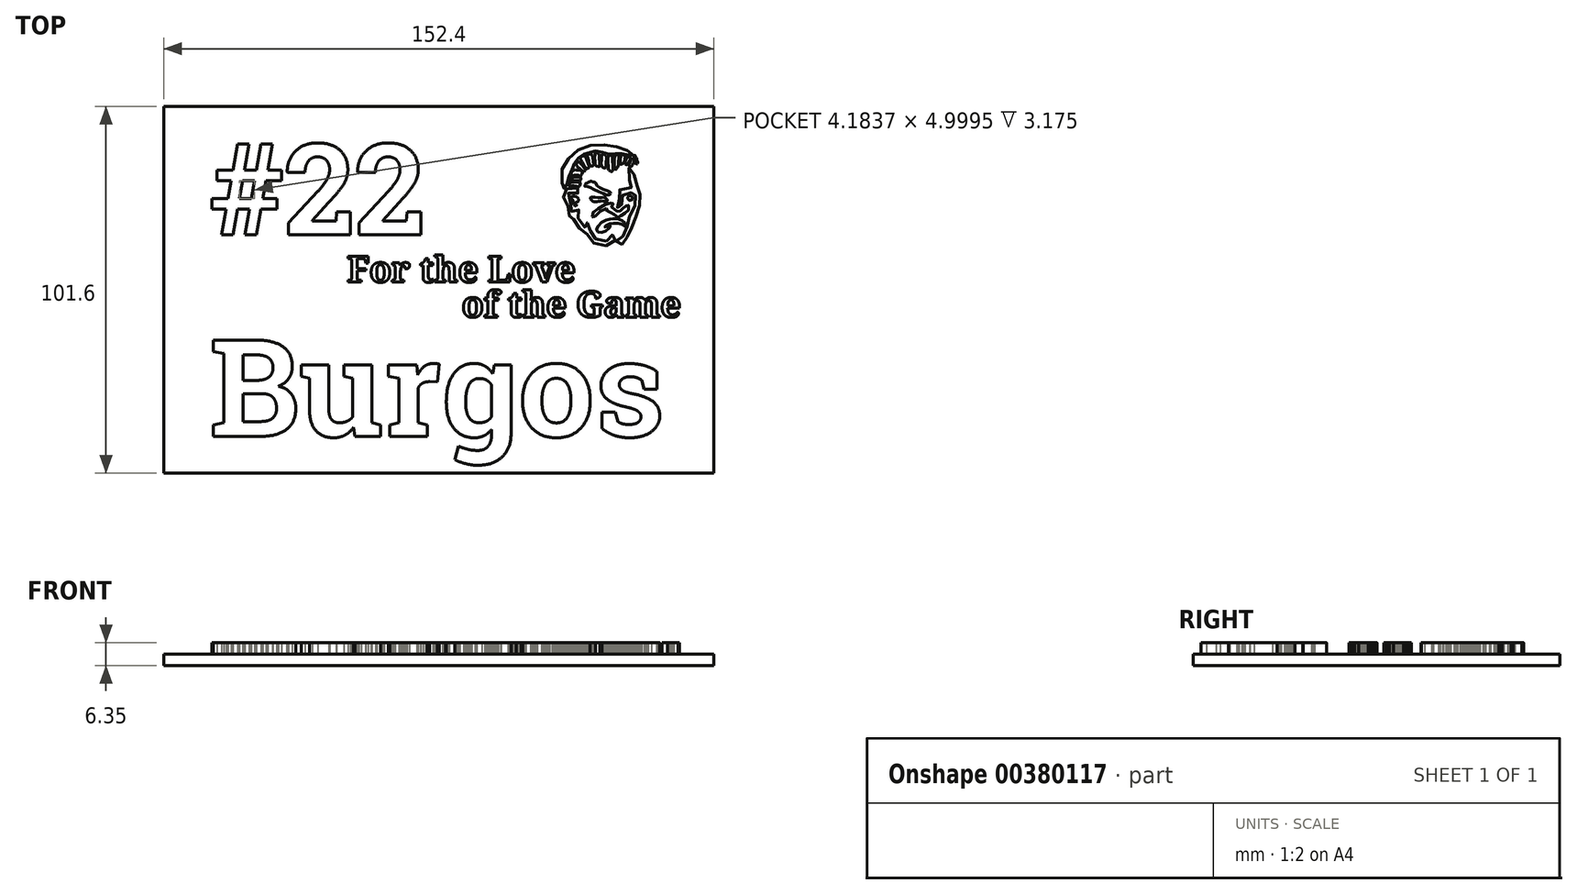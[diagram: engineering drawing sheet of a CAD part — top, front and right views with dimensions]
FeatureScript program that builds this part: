
annotation { "Feature Type Name" : "Feature", "Feature Type Description" : "" }
export const myFeature = defineFeature(function(context is Context, id is Id, definition is map)
    precondition{}
    {
        {
            var Q0;
            Q0=qCreatedBy(makeId("Top.planeOp"),FACE);
            var sketch = newSketch(context, id + "F0", { "sketchPlane" : qUnion([Q0])});
            skLineSegment(sketch, "E0.bottom", {"start": v(-75.13, 26) * mm, "end": v(77.27, 26) * mm});
            skLineSegment(sketch, "E0.top", {"start": v(-75.13, -75.6) * mm, "end": v(77.27, -75.6) * mm});
            skLineSegment(sketch, "E0.left", {"start": v(-75.13, 26) * mm, "end": v(-75.13, -75.6) * mm});
            skLineSegment(sketch, "E0.right", {"start": v(77.27, 26) * mm, "end": v(77.27, -75.6) * mm});
            skSolve(sketch);
        }
        {
            var Q0;
            Q0=makeQuery(id+"F0.imprint","IMPRINT",FACE,{"disambiguationData":[TD([[makeQuery(id+"F0.imprint","IMPRINT",EDGE,{"derivedFrom":sQuery(id+"F0.wireOp",EDGE,"E0.bottom")}),-1.0]])]});
            var sketch = newSketch(context, id + "F1", { "sketchPlane" : qUnion([Q0])});
            skText(sketch, "E1", { "text": "Burgos", "fontName": "RobotoSlab-Bold.ttf"});
            skText(sketch, "E2", { "text": "#22", "fontName": "RobotoSlab-Bold.ttf"});
            skFitSpline(sketch, "E3", {"points": [v(47.57, -11.3) * mm, v(48.35, -11.04) * mm, v(48.7, -10.35) * mm, v(49.04, -9.7) * mm, v(49.57, -9.46) * mm, v(50.02, -9.78) * mm, v(50.06, -10.58) * mm, v(49.74, -11.5) * mm, v(49.1, -12.15) * mm, v(47.63, -12.55) * mm, v(46.12, -12.5) * mm, v(44.61, -12.12) * mm, v(43.38, -11.34) * mm, v(42.6, -10.32) * mm, v(42.24, -9.52) * mm, v(42.15, -9.31) * mm, v(41.34, -8.82) * mm, v(40.33, -8.02) * mm, v(39.44, -7.2) * mm, v(38.67, -6.1) * mm, v(38.42, -5) * mm, v(38.42, -4.22) * mm, v(38.35, -4.2) * mm, v(37.68, -4.39) * mm, v(37.16, -4.27) * mm, v(36.95, -3.72) * mm, v(36.86, -2.5) * mm, v(36.8, -1.48) * mm, v(36.67, -1.07) * mm, v(35.77, 0.2) * mm, v(35.58, 1.07) * mm, v(35.86, 2.13) * mm, v(36.18, 2.7) * mm, v(36.53, 3.12) * mm, v(37.23, 3.22) * mm, v(39.03, 3.4) * mm, v(39.82, 3.34) * mm, v(40.19, 3.09) * mm, v(40.23, 2.45) * mm, v(39.66, 1.98) * mm, v(38.93, 1.9) * mm, v(38.59, 2.03) * mm, v(37.24, 2.03) * mm, v(36.72, 1.65) * mm, v(36.72, 0.85) * mm, v(37.32, -0.2) * mm, v(37.77, -1.18) * mm, v(37.85, -2.09) * mm, v(37.9, -3.1) * mm, v(37.99, -3.1) * mm, v(38.63, -3.1) * mm, v(39.4, -2.76) * mm, v(39.72, -2.59) * mm, v(39.8, -2.7) * mm, v(39.73, -3.22) * mm, v(39.6, -4) * mm, v(39.6, -4.77) * mm, v(40.1, -5.82) * mm, v(41.16, -7.15) * mm, v(41.6, -7.53) * mm, v(41.9, -7.56) * mm, v(41.89, -7.44) * mm, v(41.82, -6.61) * mm, v(42, -6.23) * mm, v(42.5, -6.3) * mm, v(42.8, -6.61) * mm, v(43.05, -7.98) * mm, v(43.22, -8.82) * mm, v(43.51, -9.54) * mm, v(44.12, -10.4) * mm, v(45.11, -11.01) * mm, v(46.32, -11.33) * mm, v(47.57, -11.3) * mm]});
            skFitSpline(sketch, "E4", {"points": [v(47.8, -7.3) * mm, v(47.13, -7.42) * mm, v(47.01, -7.42) * mm, v(47.13, -7.18) * mm, v(48.11, -6.65) * mm, v(49.11, -6.46) * mm, v(50.54, -6.45) * mm, v(51.76, -6.67) * mm, v(52.61, -7.21) * mm, v(52.82, -7.33) * mm, v(52.97, -7.12) * mm, v(52.7, -6.5) * mm, v(52.11, -5.74) * mm, v(50.6, -5.18) * mm, v(49.08, -5.16) * mm, v(48.46, -5.24) * mm, v(47.16, -5.6) * mm, v(45.65, -6.61) * mm, v(44.86, -7.78) * mm, v(44.9, -8.5) * mm, v(45.47, -8.94) * mm, v(46.7, -8.8) * mm, v(47.75, -8.16) * mm, v(48.56, -7.4) * mm, v(48.6, -7.12) * mm, v(47.8, -7.3) * mm]});
            skFitSpline(sketch, "E5", {"points": [v(51.85, -12.22) * mm, v(51.05, -12.44) * mm, v(50.33, -12.28) * mm, v(50.13, -11.73) * mm, v(50.52, -11.04) * mm, v(51.15, -10.86) * mm, v(51.76, -10.57) * mm, v(52.13, -10) * mm, v(52.3, -9.2) * mm, v(52.67, -8.25) * mm, v(53.2, -7.5) * mm, v(53.55, -6.76) * mm, v(53.63, -5.82) * mm, v(53.78, -4.85) * mm, v(54.49, -3.73) * mm, v(55.3, -2.73) * mm, v(55.42, -1.6) * mm, v(55.17, -0.4) * mm, v(55.2, 0.11) * mm, v(55.52, 1.32) * mm, v(55.57, 2.16) * mm, v(55.47, 2.42) * mm, v(54.99, 2.38) * mm, v(54.56, 2.14) * mm, v(53.7, 2.1) * mm, v(52.55, 2.06) * mm, v(52.07, 1.77) * mm, v(51.98, 1.02) * mm, v(52.2, 0.28) * mm, v(52.08, -0.6) * mm, v(51.72, -1.24) * mm, v(51.47, -1.75) * mm, v(51.5, -2.22) * mm, v(51.32, -2.4) * mm, v(50.6, -2.13) * mm, v(50.38, -1.6) * mm, v(50.64, -0.97) * mm, v(51, -0.17) * mm, v(51.06, 0.44) * mm, v(50.78, 1.07) * mm, v(50.66, 1.97) * mm, v(51.18, 2.9) * mm, v(52.12, 3.24) * mm, v(53.3, 3.36) * mm, v(54.52, 3.48) * mm, v(54.66, 3.6) * mm, v(54.38, 3.97) * mm, v(54, 4.8) * mm, v(53.79, 6.28) * mm, v(53.9, 7.94) * mm, v(53.79, 8.9) * mm, v(53.79, 9.1) * mm, v(54.03, 9.04) * mm, v(54.76, 8.52) * mm, v(55.13, 7.38) * mm, v(55.34, 5.97) * mm, v(55.56, 4.72) * mm, v(56.14, 3.87) * mm, v(56.71, 3.56) * mm, v(57.08, 2.91) * mm, v(56.95, 1.93) * mm, v(56.51, 0.55) * mm, v(56.4, -0.31) * mm, v(56.62, -1.36) * mm, v(56.69, -2.19) * mm, v(56.32, -3.56) * mm, v(55.4, -4.86) * mm, v(54.62, -5.8) * mm, v(54.5, -7.08) * mm, v(54.37, -8.24) * mm, v(53.76, -9.26) * mm, v(53.43, -9.82) * mm, v(53.28, -10.59) * mm, v(53.14, -11.27) * mm, v(52.34, -11.95) * mm, v(51.85, -12.22) * mm]});
            skFitSpline(sketch, "E6", {"points": [v(51.65, -4.28) * mm, v(52.13, -3.81) * mm, v(53.02, -3.37) * mm, v(53.66, -2.72) * mm, v(53.77, -1.9) * mm, v(53.38, -1.13) * mm, v(53.21, -1.15) * mm, v(53, -1.68) * mm, v(52.43, -2.14) * mm, v(51.8, -2.46) * mm, v(51.42, -2.92) * mm, v(50.93, -3.27) * mm, v(50.6, -3.17) * mm, v(50.13, -2.68) * mm, v(49.7, -2.46) * mm, v(49.28, -2.45) * mm, v(49, -1.98) * mm, v(49.06, -1.41) * mm, v(49.39, -0.94) * mm, v(49.4, -0.71) * mm, v(48.82, -0.74) * mm, v(47.56, -0.99) * mm, v(45.6, -2.02) * mm, v(44.06, -3.24) * mm, v(43.57, -3.77) * mm, v(43.7, -4.86) * mm, v(43.9, -4.88) * mm, v(44.45, -4.27) * mm, v(46.1, -2.93) * mm, v(47.41, -2.3) * mm, v(47.63, -2.3) * mm, v(47.73, -2.85) * mm, v(48.15, -3.33) * mm, v(48.9, -3.44) * mm, v(49.24, -3.55) * mm, v(49.84, -4.18) * mm, v(50.54, -4.68) * mm, v(51.18, -4.66) * mm, v(51.65, -4.28) * mm]});
            skFitSpline(sketch, "E7", {"points": [v(54.73, 0.39) * mm, v(54.77, 0.82) * mm, v(54.18, 1.2) * mm, v(53.55, 1.02) * mm, v(53.47, 0.3) * mm, v(54.02, 0) * mm, v(54.73, 0.39) * mm]});
            skFitSpline(sketch, "E8", {"points": [v(44.44, -0.47) * mm, v(43.66, -0.25) * mm, v(43.08, 0.44) * mm, v(43.14, 0.75) * mm, v(43.78, 0.8) * mm, v(46.74, 0.78) * mm, v(47.17, 0.7) * mm, v(47.78, -0.13) * mm, v(47.64, -0.32) * mm, v(46.64, -0.26) * mm, v(45.29, -0.32) * mm, v(44.44, -0.47) * mm]});
            skFitSpline(sketch, "E9", {"points": [v(46.65, 1.86) * mm, v(47.46, 1.48) * mm, v(48.33, 1.53) * mm, v(48.69, 2.02) * mm, v(48.54, 2.32) * mm, v(47.26, 2.83) * mm, v(45.32, 3.72) * mm, v(44.79, 4.23) * mm, v(44.53, 4.83) * mm, v(44.13, 5) * mm, v(43.88, 5) * mm, v(43.34, 5.26) * mm, v(43.09, 5.3) * mm, v(42.9, 5.05) * mm, v(42.6, 5.07) * mm, v(42.3, 4.85) * mm, v(42.2, 4.73) * mm, v(41.9, 4.72) * mm, v(41.8, 4.5) * mm, v(41.38, 4.05) * mm, v(41.56, 3.84) * mm, v(42.59, 3.74) * mm, v(43.78, 3.19) * mm, v(46.65, 1.86) * mm]});
            skFitSpline(sketch, "E10", {"points": [v(39.09, -1.2) * mm, v(38.85, -1.02) * mm, v(39.04, -0.63) * mm, v(39.6, -0.4) * mm, v(39.72, 0.33) * mm, v(39.01, 1.06) * mm, v(38.23, 1.1) * mm, v(37.7, 0.65) * mm, v(37.83, 0.29) * mm, v(38.12, 0.15) * mm, v(38.31, -0.34) * mm, v(38.52, -1.23) * mm, v(38.92, -1.63) * mm, v(39.18, -1.51) * mm, v(39.26, -1.2) * mm, v(39.09, -1.2) * mm]});
            skFitSpline(sketch, "E11", {"points": [v(35.18, 4.73) * mm, v(35.4, 3.4) * mm, v(35.76, 3.05) * mm, v(35.87, 3.13) * mm, v(36.08, 3.42) * mm, v(36.43, 3.67) * mm, v(36.66, 4.42) * mm, v(36.6, 5.36) * mm, v(37.02, 6.1) * mm, v(37.15, 6.7) * mm, v(37.23, 7.46) * mm, v(37.88, 8.4) * mm, v(38.45, 9.02) * mm, v(38.56, 9.75) * mm, v(38.74, 10.4) * mm, v(39.17, 10.98) * mm, v(39.64, 11.29) * mm, v(39.78, 11.9) * mm, v(40.12, 12.28) * mm, v(40.85, 12.68) * mm, v(41.65, 12.77) * mm, v(42.03, 12.99) * mm, v(42.91, 13.25) * mm, v(43.49, 13.17) * mm, v(43.91, 13.25) * mm, v(44.22, 13.54) * mm, v(44.87, 13.6) * mm, v(45.62, 13.32) * mm, v(46.3, 13.31) * mm, v(46.91, 13.3) * mm, v(47.51, 12.81) * mm, v(48.11, 12.71) * mm, v(48.8, 12.83) * mm, v(49.39, 12.68) * mm, v(50.13, 12.89) * mm, v(50.83, 12.96) * mm, v(51.35, 12.83) * mm, v(51.87, 12.94) * mm, v(52.53, 12.95) * mm, v(53.18, 12.6) * mm, v(53.93, 12.6) * mm, v(54.48, 12.4) * mm, v(54.65, 12.18) * mm, v(55.03, 12.55) * mm, v(54.73, 12.89) * mm, v(53.9, 13.45) * mm, v(51.53, 14.51) * mm, v(50.44, 14.76) * mm, v(49.1, 15.08) * mm, v(45.83, 15.4) * mm, v(43.17, 15.22) * mm, v(40.97, 14.54) * mm, v(38.6, 13.18) * mm, v(36.98, 11.4) * mm, v(35.34, 9.1) * mm, v(35.2, 8.1) * mm, v(35.18, 4.73) * mm]});
            skFitSpline(sketch, "E12", {"points": [v(39.4, 5) * mm, v(39.96, 4.99) * mm, v(40.23, 4.82) * mm, v(40.1, 4) * mm, v(39.64, 3.78) * mm, v(38.94, 3.9) * mm, v(37.89, 3.94) * mm, v(37.45, 3.8) * mm, v(37.1, 4.04) * mm, v(37.54, 4.84) * mm, v(38.3, 5) * mm, v(39.4, 5) * mm]});
            skFitSpline(sketch, "E13", {"points": [v(37.48, 5.07) * mm, v(37.11, 4.96) * mm, v(36.94, 5.2) * mm, v(37.34, 5.9) * mm, v(37.75, 6.14) * mm, v(39.96, 6.47) * mm, v(40.35, 6.2) * mm, v(40.47, 5.65) * mm, v(40.11, 5.36) * mm, v(39.64, 5.4) * mm, v(38.37, 5.41) * mm, v(37.48, 5.07) * mm]});
            skFitSpline(sketch, "E14", {"points": [v(38.14, 6.82) * mm, v(39.68, 6.88) * mm, v(40, 6.74) * mm, v(40.54, 7) * mm, v(40.85, 7.85) * mm, v(40.67, 8.1) * mm, v(39.1, 8.4) * mm, v(38.41, 8.3) * mm, v(37.9, 7.73) * mm, v(37.48, 6.86) * mm, v(37.68, 6.74) * mm, v(38.14, 6.82) * mm]});
            skFitSpline(sketch, "E15", {"points": [v(39.26, 9.59) * mm, v(41, 8.1) * mm, v(41.32, 7.94) * mm, v(41.68, 8.33) * mm, v(41.53, 8.74) * mm, v(40.44, 10.1) * mm, v(39.87, 10.6) * mm, v(39.5, 10.56) * mm, v(39.13, 10.09) * mm, v(39.26, 9.59) * mm]});
            skFitSpline(sketch, "E16", {"points": [v(40.75, 10.65) * mm, v(40.33, 11.47) * mm, v(40.46, 11.98) * mm, v(41.21, 12.34) * mm, v(41.77, 12.07) * mm, v(42.13, 11.12) * mm, v(42.72, 9.33) * mm, v(42.65, 8.96) * mm, v(42.12, 8.81) * mm, v(41.62, 9.07) * mm, v(40.75, 10.65) * mm]});
            skFitSpline(sketch, "E17", {"points": [v(42.43, 11.4) * mm, v(42.21, 12.24) * mm, v(42.3, 12.64) * mm, v(43, 12.81) * mm, v(43.54, 12.53) * mm, v(43.83, 11.13) * mm, v(44, 9.88) * mm, v(43.65, 9.47) * mm, v(42.94, 9.8) * mm, v(42.43, 11.4) * mm]});
            skFitSpline(sketch, "E18", {"points": [v(44.29, 12.06) * mm, v(44.36, 12.96) * mm, v(44.5, 13.26) * mm, v(44.93, 13.17) * mm, v(45.54, 12.55) * mm, v(45.55, 11.97) * mm, v(45.6, 9.45) * mm, v(45.5, 9.32) * mm, v(44.61, 9.6) * mm, v(44.4, 10.08) * mm, v(44.29, 12.06) * mm]});
            skFitSpline(sketch, "E19", {"points": [v(46.05, 10.51) * mm, v(46.15, 9.53) * mm, v(46.62, 9.04) * mm, v(47.1, 8.88) * mm, v(47.3, 9.08) * mm, v(47.48, 10.9) * mm, v(47.53, 12.07) * mm, v(47.34, 12.46) * mm, v(46.68, 12.84) * mm, v(46.32, 12.79) * mm, v(46.17, 11.97) * mm, v(46.05, 10.51) * mm]});
            skFitSpline(sketch, "E20", {"points": [v(48.03, 8.99) * mm, v(48.11, 8.48) * mm, v(48.48, 8.11) * mm, v(48.94, 7.92) * mm, v(49.21, 8.2) * mm, v(49.24, 10.23) * mm, v(49.16, 12.1) * mm, v(48.83, 12.47) * mm, v(48.44, 12.47) * mm, v(47.98, 12) * mm, v(47.93, 10.87) * mm, v(48.03, 8.99) * mm]});
            skFitSpline(sketch, "E21", {"points": [v(49.71, 9.45) * mm, v(49.86, 8.66) * mm, v(50.13, 8.48) * mm, v(50.3, 8.75) * mm, v(50.76, 9.43) * mm, v(50.85, 10.13) * mm, v(50.93, 12.16) * mm, v(50.81, 12.6) * mm, v(50.31, 12.66) * mm, v(49.83, 12.22) * mm, v(49.7, 11.19) * mm, v(49.71, 9.45) * mm]});
            skFitSpline(sketch, "E22", {"points": [v(51.32, 10.54) * mm, v(51.4, 11.84) * mm, v(51.7, 12.52) * mm, v(52.3, 12.55) * mm, v(52.72, 12.21) * mm, v(52.63, 11.54) * mm, v(52.29, 10.26) * mm, v(51.93, 10.06) * mm, v(51.44, 9.99) * mm, v(51.32, 10.54) * mm]});
            skFitSpline(sketch, "E23", {"points": [v(52.63, 10.38) * mm, v(52.83, 11.01) * mm, v(53.35, 11.9) * mm, v(53.66, 12.08) * mm, v(54.13, 11.71) * mm, v(53.9, 10.95) * mm, v(53.35, 10.1) * mm, v(53.17, 9.86) * mm, v(52.8, 9.99) * mm, v(52.63, 10.38) * mm]});
            skFitSpline(sketch, "E24", {"points": [v(53.86, 10.18) * mm, v(53.7, 9.9) * mm, v(53.81, 9.57) * mm, v(54.15, 9.28) * mm, v(54.42, 9.39) * mm, v(55.14, 10.6) * mm, v(55.26, 11.14) * mm, v(55.02, 11.54) * mm, v(54.8, 11.61) * mm, v(54.48, 11.27) * mm, v(53.86, 10.18) * mm]});
            skFitSpline(sketch, "E25", {"points": [v(55.24, 11.7) * mm, v(55.54, 11.38) * mm, v(55.58, 10.83) * mm, v(55.47, 10.49) * mm, v(55.7, 10.04) * mm, v(55.92, 10.02) * mm, v(56.2, 10.63) * mm, v(56.05, 10.85) * mm, v(55.85, 11.61) * mm, v(55.63, 12) * mm, v(55.42, 12.46) * mm, v(55.15, 12.4) * mm, v(55.09, 11.93) * mm, v(55.24, 11.7) * mm]});
            skText(sketch, "E26", { "text": "For the Love", "fontName": "NotoSerif-Bold.ttf"});
            skText(sketch, "E27", { "text": "of the Game", "fontName": "NotoSerif-Bold.ttf"});
            const initialGuessF1  = {"E1": [-0.06243, -0.06544, 1, 0, 0.02705], "E2": [-0.06243, -0.00956, 1, 0, 0.0254], "E26": [-0.02433, -0.0227, 1, 0, 0.00716], "E27": [0.00742, -0.0324, 1, 0, 0.00716]};
            skSetInitialGuess(sketch, initialGuessF1);
            skSolve(sketch);
        }
        {
            var Q0;
            Q0 = qSketchRegion(id + "F0", true);
            extrude(context, id + "F2", {"entities" : qUnion([Q0]), "depth" : 3.17 * mm});
        }
        {
            var Q0;
            Q0 = qSketchRegion(id + "F1", true);
            extrude(context, id + "F3", {"entities" : qUnion([Q0]), "operationType" : NewBodyOperationType.ADD, "depth" : 6.35 * mm});
        }
    });
